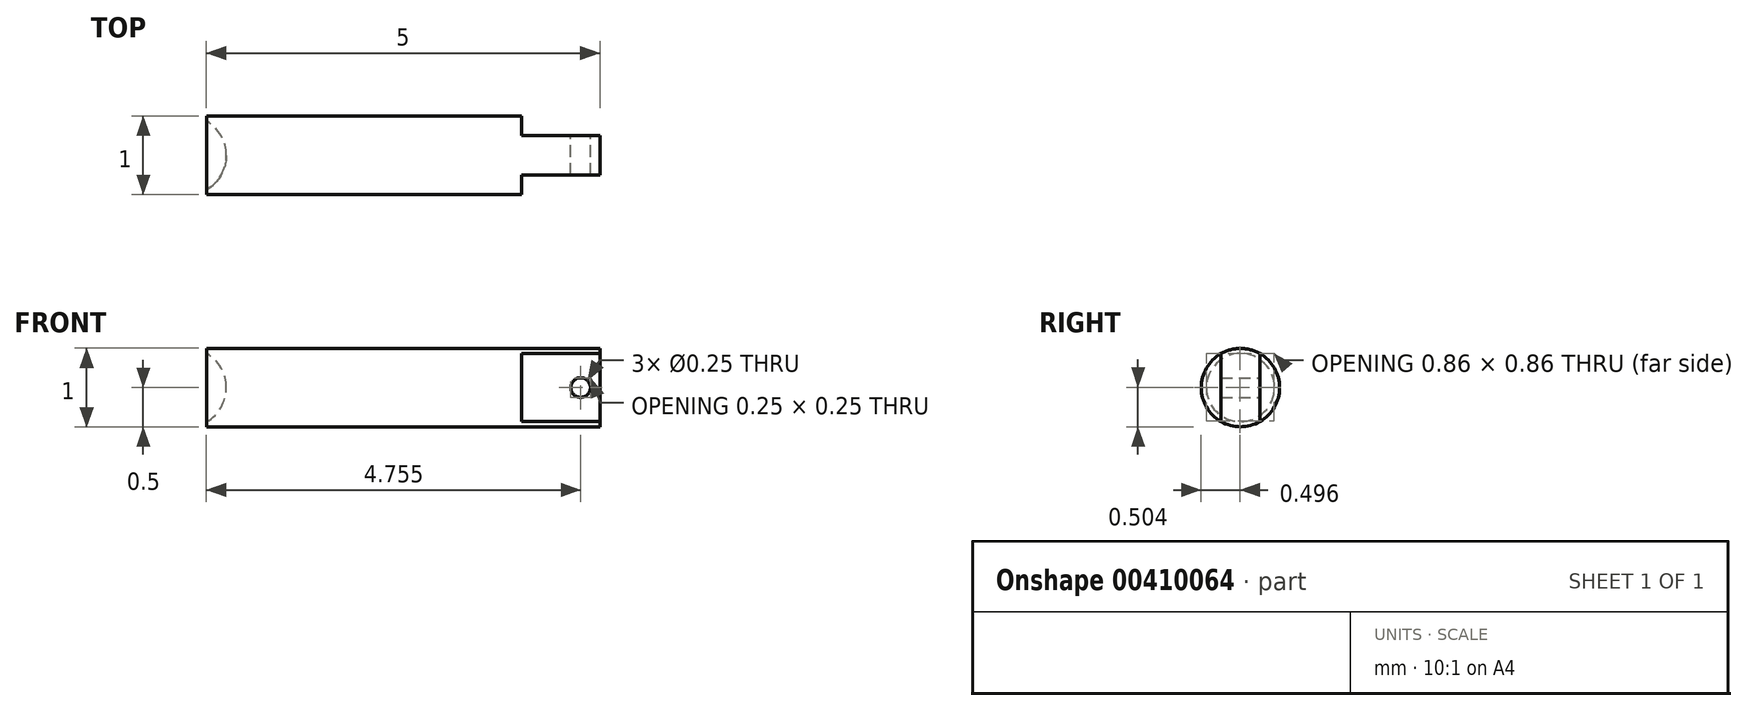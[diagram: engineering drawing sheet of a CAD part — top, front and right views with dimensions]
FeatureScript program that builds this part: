
annotation { "Feature Type Name" : "Feature", "Feature Type Description" : "" }
export const myFeature = defineFeature(function(context is Context, id is Id, definition is map)
    precondition{}
    {
        {
            var Q0;
            Q0=qCreatedBy(makeId("Top.planeOp"),FACE);
            var sketch = newSketch(context, id + "F0", { "sketchPlane" : qUnion([Q0])});
            skLineSegment(sketch, "E0", {"start": v(-2.82, 0) * mm, "end": v(3.1, 0) * mm, "construction": true});
            skArc(sketch, "E1", {"start": v(-1.75, 0) * mm, "mid": v(-1.81, 0.25) * mm, "end": v(-2, 0.43) * mm});
            skLineSegment(sketch, "E2.bottom", {"start": v(-2, 0) * mm, "end": v(3, 0) * mm});
            skLineSegment(sketch, "E2.top", {"start": v(-2, 0.5) * mm, "end": v(3, 0.5) * mm});
            skLineSegment(sketch, "E2.left", {"start": v(-2, 0.43) * mm, "end": v(-2, 0.5) * mm});
            skLineSegment(sketch, "E2.right", {"start": v(3, 0) * mm, "end": v(3, 0.5) * mm});
            skSolve(sketch);
        }
        {
            var Q0;
            {var subQ1=sQuery(id+"F0.wireOp",EDGE,"E1");Q0=makeQuery(id+"F0.imprint","IMPRINT",FACE,{"disambiguationData":[TD([[makeQuery(id+"F0.imprint","IMPRINT",EDGE,{"derivedFrom":subQ1}),-1.0]])]});}
            var Q1;
            Q1=sQuery(id+"F0.wireOp",EDGE,"E2.bottom");
            revolve(context, id + "F1", {"entities" : qUnion([Q0]), "axis" : qUnion([Q1]), "revolveType" : RevolveType.FULL});
        }
        {
            var Q0;
            Q0=qCreatedBy(makeId("Top.planeOp"),FACE);
            var sketch = newSketch(context, id + "F2", { "sketchPlane" : qUnion([Q0])});
            skLineSegment(sketch, "E3.bottom", {"start": v(2, 0.63) * mm, "end": v(3, 0.63) * mm});
            skLineSegment(sketch, "E3.top", {"start": v(2, 0.25) * mm, "end": v(3, 0.25) * mm});
            skLineSegment(sketch, "E3.left", {"start": v(2, 0.63) * mm, "end": v(2, 0.25) * mm});
            skLineSegment(sketch, "E3.right", {"start": v(3, 0.63) * mm, "end": v(3, 0.25) * mm});
            skLineSegment(sketch, "E4.MirrorCS", {"start": v(2, -0.63) * mm, "end": v(3, -0.63) * mm});
            skLineSegment(sketch, "E5.MirrorCS", {"start": v(3, -0.63) * mm, "end": v(3, -0.25) * mm});
            skLineSegment(sketch, "E6.MirrorCS", {"start": v(2, -0.25) * mm, "end": v(3, -0.25) * mm});
            skLineSegment(sketch, "E7.MirrorCS", {"start": v(2, -0.63) * mm, "end": v(2, -0.25) * mm});
            skSolve(sketch);
        }
        {
            var Q0;
            Q0=makeQuery(id+"F2.imprint","IMPRINT",FACE,{"disambiguationData":[TD([[makeQuery(id+"F2.imprint","IMPRINT",EDGE,{"derivedFrom":sQuery(id+"F2.wireOp",EDGE,"E3.bottom")}),-1.0]])]});
            var Q1;
            Q1=makeQuery(id+"F2.imprint","IMPRINT",FACE,{"disambiguationData":[TD([[makeQuery(id+"F2.imprint","IMPRINT",EDGE,{"derivedFrom":sQuery(id+"F2.wireOp",EDGE,"E4.MirrorCS")}),1.0]])]});
            extrude(context, id + "F3", {"entities" : qUnion([Q0, Q1]), "operationType" : NewBodyOperationType.REMOVE, "endBound" : BoundingType.SYMMETRIC, "oppositeDirection" : true, "depth" : 25 * mm});
        }
        {
            var Q0;
            Q0=makeQuery(id+"F3.boolean.opBoolean","COPY",FACE,{"derivedFrom":makeQuery(id+"F3.opExtrude","SWEPT_FACE",FACE,{"disambiguationData":[OSD([sQuery(id+"F2.wireOp",EDGE,"E3.top")])]})});
            var sketch = newSketch(context, id + "F4", { "sketchPlane" : qUnion([Q0])});
            skCircle(sketch, "E8", {"center": v(-2.75, 0) * mm, "radius": 0.12 * mm});
            skSolve(sketch);
        }
        {
            var Q0;
            Q0 = qSketchRegion(id + "F4", true);
            extrude(context, id + "F5", {"entities" : qUnion([Q0]), "operationType" : NewBodyOperationType.REMOVE, "oppositeDirection" : true, "depth" : 25 * mm});
        }
    });
